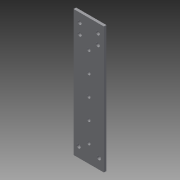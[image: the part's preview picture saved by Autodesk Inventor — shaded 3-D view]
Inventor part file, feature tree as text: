
AUTODESK INVENTOR PART (.ipt)
format: ipt  version: 2014 (Build 180170000, 170)  size: 98,816 bytes
history: native  units: in
note: dims shown in document units (in); Inventor stores cm internally (conversion verified against a paired STEP export)
features: extrude x1, sketch x1
ambient origin geometry x8: Origin, YZ Plane, XZ Plane, XY Plane, X Axis, Y Axis, Z Axis, Center Point
bodies: Solid1 (feature_tree)
feature tree (2):
  extrude  "Extrusion1"  Depth=0.125in
  sketch  "Sketch1"  dims[d0=0.192in d1=6.25in d2=0.5in d3=0.5in d4=0.5in d5=0.4485in d6=4.817in d7=1.5in d8=1.0in d9=1.375in d10=4.0in d11=0.164in d12=1.9685in d14=1.0in d15=0.3937in d17=1.0in d19=0.125in d20=0.0in]
